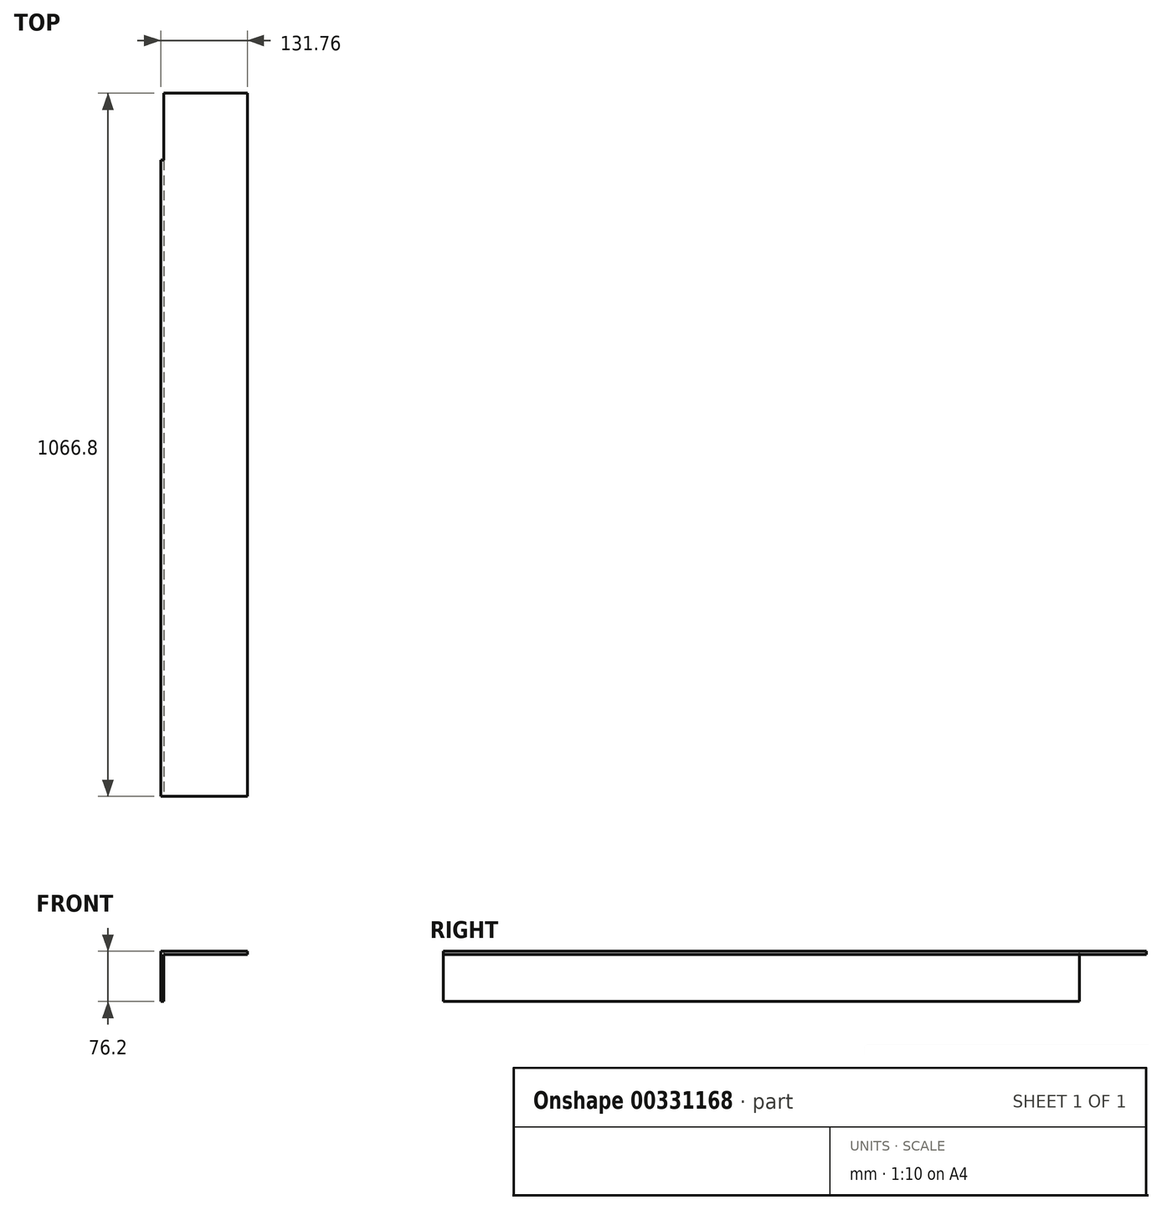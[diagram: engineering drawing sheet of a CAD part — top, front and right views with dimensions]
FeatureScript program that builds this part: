
annotation { "Feature Type Name" : "Feature", "Feature Type Description" : "" }
export const myFeature = defineFeature(function(context is Context, id is Id, definition is map)
    precondition{}
    {
        {
            var Q0;
            Q0=qCreatedBy(makeId("Top.planeOp"),FACE);
            var sketch = newSketch(context, id + "F0", { "sketchPlane" : qUnion([Q0])});
            skLineSegment(sketch, "E0.bottom", {"start": v(63.5, 533.4) * mm, "end": v(-63.5, 533.4) * mm});
            skLineSegment(sketch, "E0.top", {"start": v(63.5, -533.4) * mm, "end": v(-63.5, -533.4) * mm});
            skLineSegment(sketch, "E0.left", {"start": v(63.5, -381) * mm, "end": v(63.5, -533.4) * mm});
            skLineSegment(sketch, "E0.right", {"start": v(-63.5, 533.4) * mm, "end": v(-63.5, -533.4) * mm});
            skPoint(sketch, "E0.middle", {"position": v(0, 0) * mm});
            skLineSegment(sketch, "E1", {"start": v(63.5, 533.4) * mm, "end": v(63.5, -381) * mm});
            skSolve(sketch);
        }
        {
            var Q0;
            Q0=qSketchRegion(id+"F0",true);
            extrude(context, id + "F1", {"entities" : qUnion([Q0]), "depth" : 4.76 * mm});
        }
        {
            var Q0;
            Q0=makeQuery(id+"F1.opExtrude","SWEPT_FACE",FACE,{"disambiguationData":[OSD([sQuery(id+"F0.wireOp",EDGE,"E0.right")])]});
            var sketch = newSketch(context, id + "F2", { "sketchPlane" : qUnion([Q0])});
            skLineSegment(sketch, "E2.bottom", {"start": v(533.4, 4.76) * mm, "end": v(-431.8, 4.76) * mm});
            skLineSegment(sketch, "E2.top", {"start": v(533.4, -71.44) * mm, "end": v(-431.8, -71.44) * mm});
            skLineSegment(sketch, "E2.left", {"start": v(533.4, 4.76) * mm, "end": v(533.4, -71.44) * mm});
            skLineSegment(sketch, "E3", {"start": v(-431.8, -71.44) * mm, "end": v(-431.8, 4.76) * mm});
            skPoint(sketch, "E2.right.start.orphan", {"position": v(-251.16, 4.76) * mm});
            skSolve(sketch);
        }
        {
            var Q0;
            Q0 = qSketchRegion(id + "F2", true);
            extrude(context, id + "F3", {"entities" : qUnion([Q0]), "operationType" : NewBodyOperationType.ADD, "depth" : 4.76 * mm});
        }
    });
